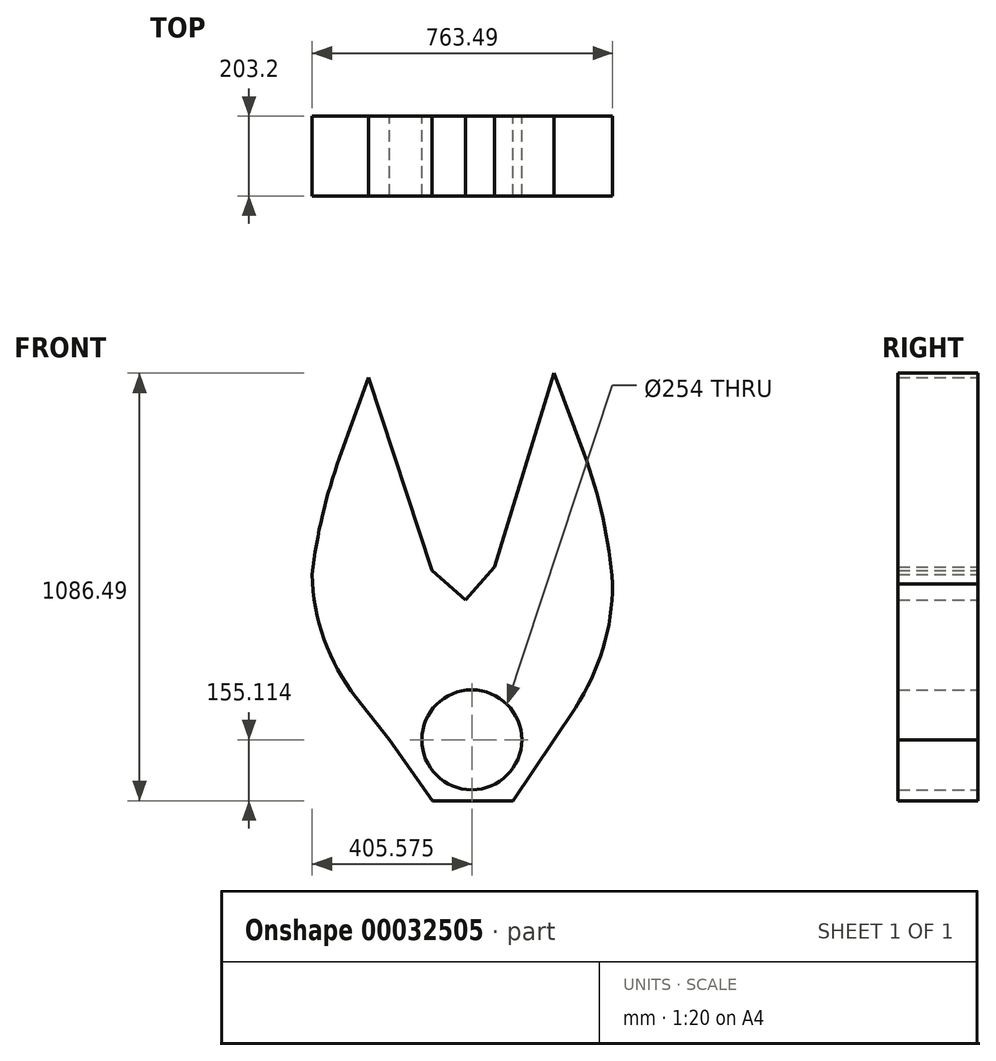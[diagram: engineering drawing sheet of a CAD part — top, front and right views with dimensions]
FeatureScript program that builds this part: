
annotation { "Feature Type Name" : "Feature", "Feature Type Description" : "" }
export const myFeature = defineFeature(function(context is Context, id is Id, definition is map)
    precondition{}
    {
        {
            var Q0;
            Q0=qCreatedBy(makeId("Front.planeOp"),FACE);
            var sketch = newSketch(context, id + "F0", { "sketchPlane" : qUnion([Q0])});
            skLineSegment(sketch, "E0.top", {"start": v(-193.34, -261.05) * mm, "end": v(225.6, -261.05) * mm});
            skLineSegment(sketch, "E1", {"start": v(-245.7, 659.11) * mm, "end": v(-84.87, 169.1) * mm});
            skLineSegment(sketch, "E2", {"start": v(-84.87, 169.1) * mm, "end": v(0, 94.3) * mm});
            skLineSegment(sketch, "E3", {"start": v(0, 94.3) * mm, "end": v(73.38, 177.55) * mm});
            skLineSegment(sketch, "E4", {"start": v(73.38, 177.55) * mm, "end": v(225.6, 670.33) * mm});
            skCircle(sketch, "E5", {"center": v(16.13, -261.05) * mm, "radius": 127 * mm});
            skLineSegment(sketch, "E6", {"start": v(-193.34, -261.05) * mm, "end": v(-83.48, -416.16) * mm});
            skLineSegment(sketch, "E7", {"start": v(-83.48, -416.16) * mm, "end": v(120.9, -416.16) * mm});
            skLineSegment(sketch, "E8", {"start": v(120.9, -416.16) * mm, "end": v(225.6, -261.05) * mm});
            skLineSegment(sketch, "E9", {"start": v(-385.9, -15.73) * mm, "end": v(-193.34, -261.05) * mm});
            skLineSegment(sketch, "E10", {"start": v(225.6, -261.05) * mm, "end": v(373.26, -36.58) * mm});
            skLineSegment(sketch, "E11", {"start": v(-245.7, 659.11) * mm, "end": v(-391.45, 258.24) * mm});
            skLineSegment(sketch, "E12", {"start": v(-391.45, 258.24) * mm, "end": v(-385.9, -15.73) * mm});
            skLineSegment(sketch, "E13", {"start": v(225.6, 670.33) * mm, "end": v(374.65, 268.65) * mm});
            skLineSegment(sketch, "E14", {"start": v(374.65, 268.65) * mm, "end": v(373.26, -36.58) * mm});
            skSolve(sketch);
        }
        {
            var Q0;
            Q0 = qSketchRegion(id + "F0", true);
            extrude(context, id + "F1", {"entities" : qUnion([Q0]), "depth" : 203.2 * mm});
        }
        {
            var Q0;
            Q0=makeQuery(id+"F1.opExtrude","SWEPT_EDGE",EDGE,{"disambiguationData":[OSD([sQuery(id+"F0.wireOp",EDGE,"E9"),sQuery(id+"F0.wireOp",EDGE,"E12")])]});
            fillet(context, id + "F2", {"entities" : qUnion([Q0]), "radius" : 524.22 * mm, "tangentPropagation" : true, "allowEdgeOverflow" : false});
        }
        {
            var Q0;
            Q0=makeQuery(id+"F1.opExtrude","SWEPT_EDGE",EDGE,{"disambiguationData":[OSD([sQuery(id+"F0.wireOp",EDGE,"E10"),sQuery(id+"F0.wireOp",EDGE,"E14")])]});
            fillet(context, id + "F3", {"entities" : qUnion([Q0]), "radius" : 576.47 * mm, "tangentPropagation" : true, "allowEdgeOverflow" : false});
        }
        {
            var Q0;
            Q0=makeQuery(id+"F1.opExtrude","SWEPT_EDGE",EDGE,{"disambiguationData":[OSD([sQuery(id+"F0.wireOp",EDGE,"E11"),sQuery(id+"F0.wireOp",EDGE,"E12")])]});
            fillet(context, id + "F4", {"entities" : qUnion([Q0]), "radius" : 1309 * mm, "tangentPropagation" : true, "allowEdgeOverflow" : false});
        }
        {
            var Q0;
            Q0=makeQuery(id+"F1.opExtrude","SWEPT_EDGE",EDGE,{"disambiguationData":[OSD([sQuery(id+"F0.wireOp",EDGE,"E13"),sQuery(id+"F0.wireOp",EDGE,"E14")])]});
            fillet(context, id + "F5", {"entities" : qUnion([Q0]), "radius" : 1218.64 * mm, "tangentPropagation" : true, "allowEdgeOverflow" : false});
        }
    });
